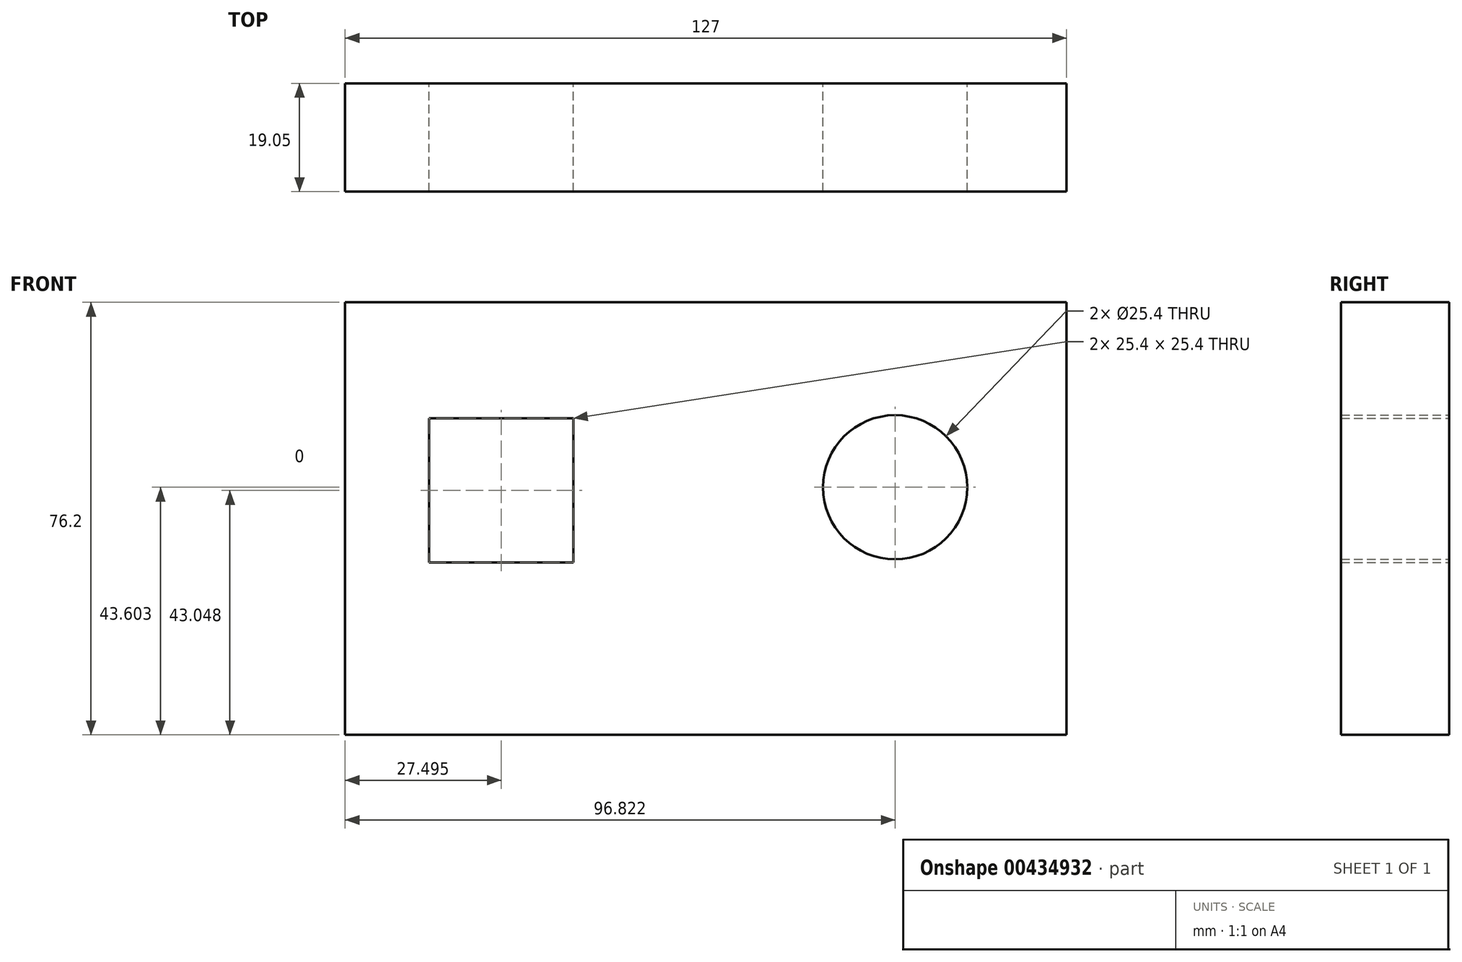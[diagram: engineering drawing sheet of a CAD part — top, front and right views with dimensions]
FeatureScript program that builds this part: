
annotation { "Feature Type Name" : "Feature", "Feature Type Description" : "" }
export const myFeature = defineFeature(function(context is Context, id is Id, definition is map)
    precondition{}
    {
        {
            var Q0;
            Q0=qCreatedBy(makeId("Front.planeOp"),FACE);
            var sketch = newSketch(context, id + "F0", { "sketchPlane" : qUnion([Q0])});
            skLineSegment(sketch, "E0.bottom", {"start": v(-62.34, -3.55) * mm, "end": v(64.66, -3.55) * mm});
            skLineSegment(sketch, "E0.top", {"start": v(-62.34, 72.65) * mm, "end": v(64.66, 72.65) * mm});
            skLineSegment(sketch, "E0.left", {"start": v(-62.34, -3.55) * mm, "end": v(-62.34, 72.65) * mm});
            skLineSegment(sketch, "E0.right", {"start": v(64.66, -3.55) * mm, "end": v(64.66, 72.65) * mm});
            skLineSegment(sketch, "E1.bottom", {"start": v(-47.54, 26.8) * mm, "end": v(-22.14, 26.8) * mm});
            skLineSegment(sketch, "E1.top", {"start": v(-47.54, 52.2) * mm, "end": v(-22.14, 52.2) * mm});
            skLineSegment(sketch, "E1.left", {"start": v(-47.54, 26.8) * mm, "end": v(-47.54, 52.2) * mm});
            skLineSegment(sketch, "E1.right", {"start": v(-22.14, 26.8) * mm, "end": v(-22.14, 52.2) * mm});
            skCircle(sketch, "E2", {"center": v(34.48, 40.05) * mm, "radius": 12.7 * mm});
            skSolve(sketch);
        }
        {
            var Q0;
            Q0=makeQuery(id+"F0.imprint","IMPRINT",FACE,{"disambiguationData":[TD([[makeQuery(id+"F0.imprint","IMPRINT",EDGE,{"derivedFrom":sQuery(id+"F0.wireOp",EDGE,"E0.bottom")}),1.0]])]});
            extrude(context, id + "F1", {"entities" : qUnion([Q0]), "depth" : 19.05 * mm});
        }
    });
